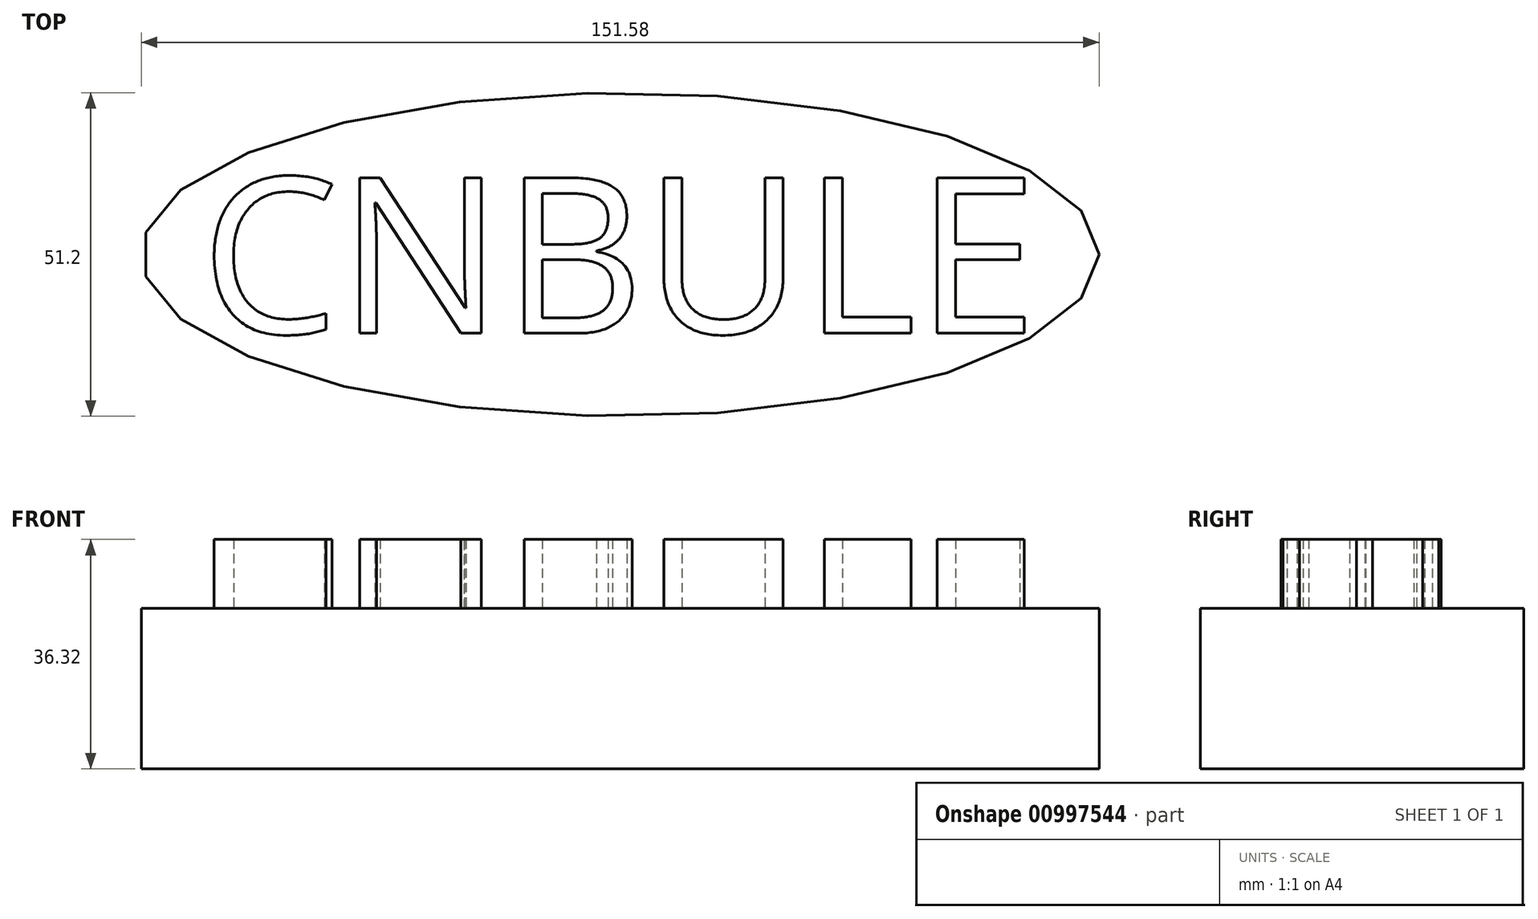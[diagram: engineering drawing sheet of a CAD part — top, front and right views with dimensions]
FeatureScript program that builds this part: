
annotation { "Feature Type Name" : "Feature", "Feature Type Description" : "" }
export const myFeature = defineFeature(function(context is Context, id is Id, definition is map)
    precondition{}
    {
        {
            var Q0;
            Q0=qCreatedBy(makeId("Top.planeOp"),FACE);
            var sketch = newSketch(context, id + "F0", { "sketchPlane" : qUnion([Q0])});
            skEllipse(sketch, "E0", {"center": v(0, 0) * mm, "majorRadius": 75.79 * mm, "minorRadius": 25.6 * mm, "majorAxis": v(1, 0)});
            skSolve(sketch);
        }
        {
            var Q0;
            Q0=makeQuery(id+"F0.imprint","IMPRINT",FACE,{"disambiguationData":[TD([[makeQuery(id+"F0.imprint","IMPRINT",EDGE,{"derivedFrom":sQuery(id+"F0.wireOp",EDGE,"E0")}),1.0]])]});
            extrude(context, id + "F1", {"entities" : qUnion([Q0]), "depth" : 25.4 * mm, "offsetDistance" : 25.4 * mm});
        }
        {
            var Q0;
            Q0=makeQuery(id+"F1.opExtrude","CAP_FACE",FACE,{"disambiguationData":[OSD([sQuery(id+"F0.wireOp",EDGE,"E0")])],"isStart":false});
            var sketch = newSketch(context, id + "F2", { "sketchPlane" : qUnion([Q0])});
            skText(sketch, "E1", { "text": "CNBULE", "fontName": "OpenSans-Regular.ttf"});
            const initialGuessF2  = {"E1": [-0.06635, -0.01247, 1, 0, 0.02484]};
            skSetInitialGuess(sketch, initialGuessF2);
            skSolve(sketch);
        }
        {
            var Q0;
            Q0 = qSketchRegion(id + "F2", true);
            extrude(context, id + "F3", {"entities" : qUnion([Q0]), "operationType" : NewBodyOperationType.ADD, "depth" : 10.92 * mm, "offsetDistance" : 25.4 * mm});
        }
    });
